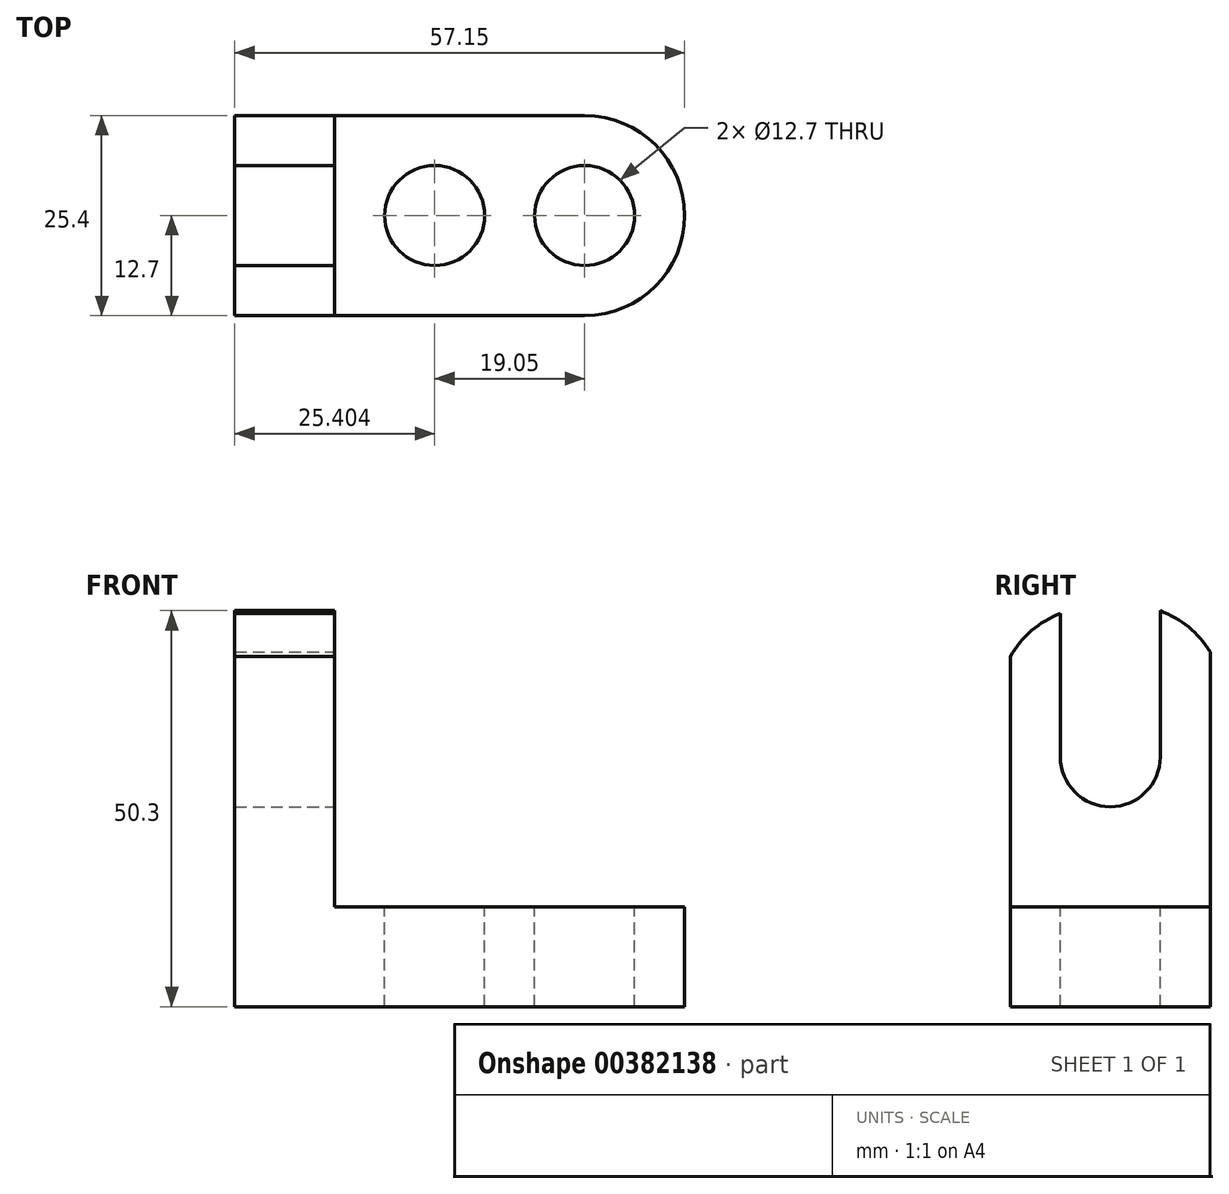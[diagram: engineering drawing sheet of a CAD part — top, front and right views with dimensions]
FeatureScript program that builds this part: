
annotation { "Feature Type Name" : "Feature", "Feature Type Description" : "" }
export const myFeature = defineFeature(function(context is Context, id is Id, definition is map)
    precondition{}
    {
        {
            var Q0;
            Q0=qCreatedBy(makeId("Front.planeOp"),FACE);
            var sketch = newSketch(context, id + "F0", { "sketchPlane" : qUnion([Q0])});
            skLineSegment(sketch, "E0", {"start": v(-68.83, 50.8) * mm, "end": v(-68.83, 0) * mm});
            skLineSegment(sketch, "E1", {"start": v(-68.83, 0) * mm, "end": v(-11.68, 0) * mm});
            skLineSegment(sketch, "E2", {"start": v(-11.68, 0) * mm, "end": v(-11.68, 12.7) * mm});
            skLineSegment(sketch, "E3", {"start": v(-11.68, 12.7) * mm, "end": v(-56.13, 12.7) * mm});
            skLineSegment(sketch, "E4", {"start": v(-56.13, 12.7) * mm, "end": v(-56.13, 50.8) * mm});
            skLineSegment(sketch, "E5", {"start": v(-68.83, 50.8) * mm, "end": v(-56.13, 50.8) * mm});
            skSolve(sketch);
        }
        {
            var Q0;
            Q0=makeQuery(id+"F0.imprint","IMPRINT",FACE,{"disambiguationData":[TD([[makeQuery(id+"F0.imprint","IMPRINT",EDGE,{"derivedFrom":sQuery(id+"F0.wireOp",EDGE,"E0")}),1.0]])]});
            extrude(context, id + "F1", {"entities" : qUnion([Q0]), "depth" : 25.4 * mm});
        }
        {
            var Q0;
            Q0=makeQuery(id+"F1.opExtrude","SWEPT_FACE",FACE,{"disambiguationData":[OSD([sQuery(id+"F0.wireOp",EDGE,"E3")])]});
            var sketch = newSketch(context, id + "F2", { "sketchPlane" : qUnion([Q0])});
            skCircle(sketch, "E6", {"center": v(-43.43, -12.7) * mm, "radius": 6.35 * mm});
            skCircle(sketch, "E7", {"center": v(-24.38, -12.7) * mm, "radius": 6.35 * mm});
            skSolve(sketch);
        }
        {
            var Q0;
            Q0=makeQuery(id+"F2.imprint","IMPRINT",FACE,{"disambiguationData":[TD([[makeQuery(id+"F2.imprint","IMPRINT",EDGE,{"derivedFrom":sQuery(id+"F2.wireOp",EDGE,"E6")}),1.0]])]});
            var Q1;
            Q1=makeQuery(id+"F2.imprint","IMPRINT",FACE,{"disambiguationData":[TD([[makeQuery(id+"F2.imprint","IMPRINT",EDGE,{"derivedFrom":sQuery(id+"F2.wireOp",EDGE,"E7")}),1.0]])]});
            extrude(context, id + "F3", {"entities" : qUnion([Q0, Q1]), "operationType" : NewBodyOperationType.REMOVE, "oppositeDirection" : true, "depth" : 12.7 * mm});
        }
        {
            var Q0;
            Q0=makeQuery(id+"F1.opExtrude","SWEPT_FACE",FACE,{"disambiguationData":[OSD([sQuery(id+"F0.wireOp",EDGE,"E3")])]});
            var sketch = newSketch(context, id + "F4", { "sketchPlane" : qUnion([Q0])});
            skArc(sketch, "E8", {"start": v(-11.68, -12.7) * mm, "mid": v(-15.4, -3.72) * mm, "end": v(-24.38, 0) * mm});
            skArc(sketch, "E9", {"start": v(-24.38, -25.4) * mm, "mid": v(-15.4, -21.68) * mm, "end": v(-11.68, -12.7) * mm});
            skSolve(sketch);
        }
        {
            var Q0;
            {var subQ0=sQuery(id+"F4.wireOp",EDGE,"E8");Q0=makeQuery(id+"F4.imprint","IMPRINT",FACE,{"disambiguationData":[TD([[makeQuery(id+"F4.imprint","IMPRINT",EDGE,{"derivedFrom":subQ0}),-1.0]])]});}
            var Q1;
            {var subQ0=sQuery(id+"F4.wireOp",EDGE,"E9");Q1=makeQuery(id+"F4.imprint","IMPRINT",FACE,{"disambiguationData":[TD([[makeQuery(id+"F4.imprint","IMPRINT",EDGE,{"derivedFrom":subQ0}),-1.0]])]});}
            extrude(context, id + "F5", {"entities" : qUnion([Q0, Q1]), "operationType" : NewBodyOperationType.REMOVE, "oppositeDirection" : true, "depth" : 25.4 * mm});
        }
        {
            var Q0;
            Q0=makeQuery(id+"F1.opExtrude","SWEPT_FACE",FACE,{"disambiguationData":[OSD([sQuery(id+"F0.wireOp",EDGE,"E4")])]});
            var sketch = newSketch(context, id + "F6", { "sketchPlane" : qUnion([Q0])});
            skCircle(sketch, "E10", {"center": v(-12.7, 31.75) * mm, "radius": 6.35 * mm});
            skLineSegment(sketch, "E11", {"start": v(-19.04, 31.75) * mm, "end": v(-19.04, 50.8) * mm});
            skLineSegment(sketch, "E12", {"start": v(-6.34, 31.75) * mm, "end": v(-6.34, 50.8) * mm});
            skLineSegment(sketch, "E13", {"start": v(-6.34, 50.8) * mm, "end": v(-19.04, 50.8) * mm});
            skSolve(sketch);
        }
        {
            var Q0;
            {var subQ0=sQuery(id+"F6.wireOp",EDGE,"E11");Q0=makeQuery(id+"F6.imprint","IMPRINT",FACE,{"disambiguationData":[TD([[makeQuery(id+"F6.imprint","IMPRINT",EDGE,{"derivedFrom":subQ0}),-1.0]])]});}
            var Q1;
            {var subQ0=sQuery(id+"F6.wireOp",EDGE,"E10");var subQ1=makeQuery(id+"F6.imprint","INTERSECT",VERTEX,{"derivedFrom":[subQ0,sQuery(id+"F6.wireOp",EDGE,"E11")]});Q1=makeQuery(id+"F6.imprint","IMPRINT",FACE,{"disambiguationData":[TD([[makeQuery(id+"F6.imprint","IMPRINT",EDGE,{"disambiguationData":[TD([[subQ1,1.0]])],"derivedFrom":subQ0}),1.0]])]});}
            extrude(context, id + "F7", {"entities" : qUnion([Q0, Q1]), "operationType" : NewBodyOperationType.REMOVE, "oppositeDirection" : true, "depth" : 12.7 * mm});
        }
        {
            var Q0;
            Q0=makeQuery(id+"F1.opExtrude","SWEPT_FACE",FACE,{"disambiguationData":[OSD([sQuery(id+"F0.wireOp",EDGE,"E4")])]});
            var sketch = newSketch(context, id + "F8", { "sketchPlane" : qUnion([Q0])});
            skArc(sketch, "E14", {"start": v(-13.62, 50.8) * mm, "mid": v(-25.22, 44.8) * mm, "end": v(-25.4, 31.75) * mm});
            skArc(sketch, "E15", {"start": v(0, 31.75) * mm, "mid": v(-0.48, 45.8) * mm, "end": v(-13.62, 50.8) * mm});
            skSolve(sketch);
        }
        {
            var Q0;
            {var subQ0=sQuery(id+"F8.wireOp",EDGE,"E14");var subQ1=sQuery(id+"F6.wireOp",EDGE,"E11");var subQ2=makeQuery(id+"F7.boolean.opBoolean","COPY",EDGE,{"derivedFrom":makeQuery(id+"F7.opExtrude","CAP_EDGE",EDGE,{"disambiguationData":[OSD([subQ1])],"isStart":true})});var subQ3=makeQuery(id+"F8.imprint","INTERSECT",VERTEX,{"derivedFrom":[subQ2,subQ0]});Q0=makeQuery(id+"F8.imprint","IMPRINT",FACE,{"disambiguationData":[TD([[makeQuery(id+"F8.imprint","IMPRINT",EDGE,{"disambiguationData":[TD([[subQ3,-1.0]])],"derivedFrom":subQ0}),-1.0]])]});}
            var Q1;
            {var subQ0=sQuery(id+"F8.wireOp",EDGE,"E15");var subQ1=sQuery(id+"F0.wireOp",EDGE,"E4");var subQ2=makeQuery(id+"F1.opExtrude","CAP_EDGE",EDGE,{"disambiguationData":[OSD([subQ1])],"isStart":true});var subQ3=makeQuery(id+"F8.imprint","INTERSECT",VERTEX,{"disambiguationData":[OD(1.0)],"derivedFrom":[subQ2,subQ0]});Q1=makeQuery(id+"F8.imprint","IMPRINT",FACE,{"disambiguationData":[TD([[makeQuery(id+"F8.imprint","IMPRINT",EDGE,{"disambiguationData":[TD([[subQ3,-1.0]])],"derivedFrom":subQ0}),-1.0]])]});}
            extrude(context, id + "F9", {"entities" : qUnion([Q0, Q1]), "operationType" : NewBodyOperationType.REMOVE, "oppositeDirection" : true, "depth" : 12.7 * mm});
        }
    });
